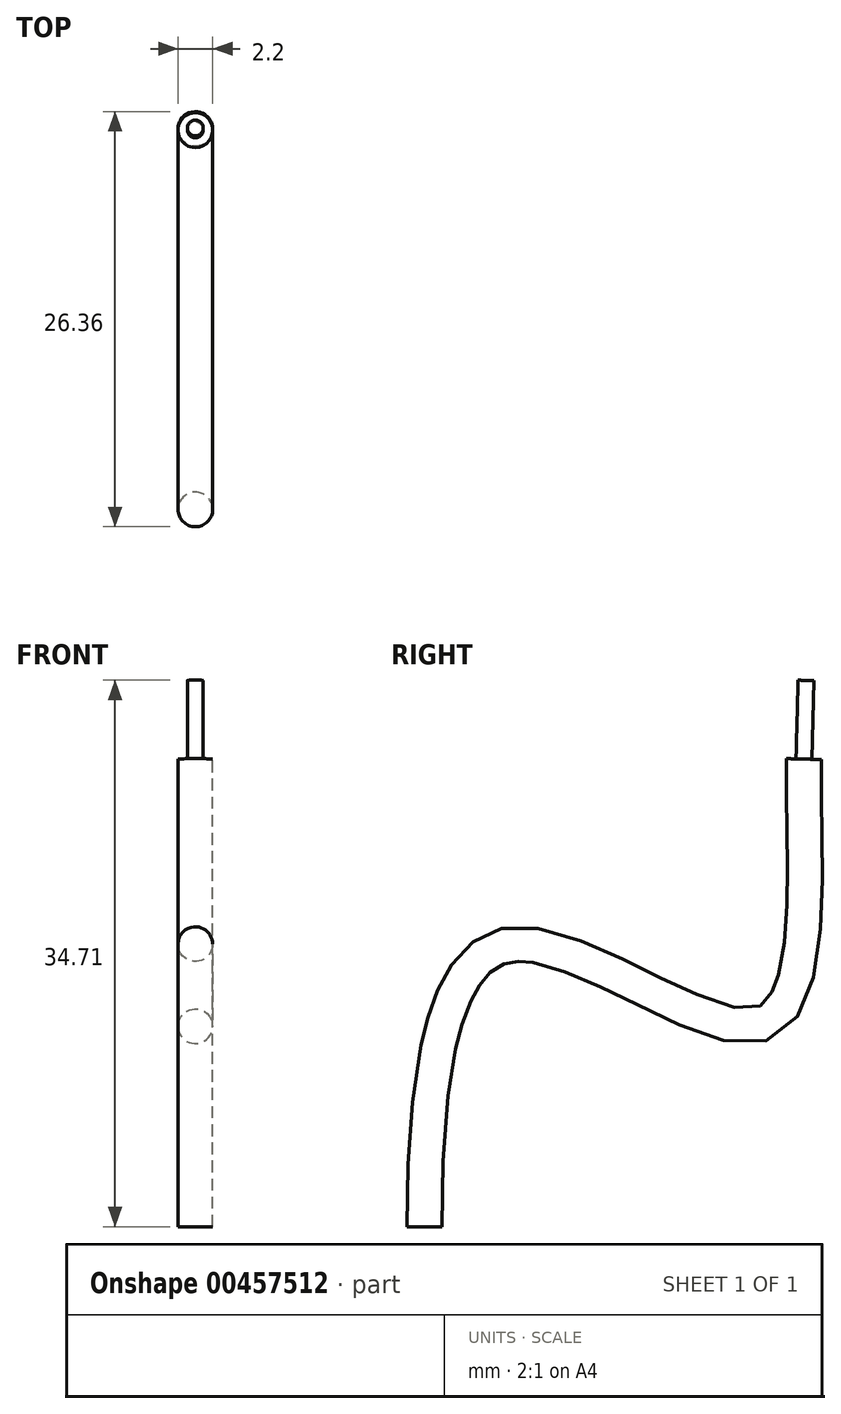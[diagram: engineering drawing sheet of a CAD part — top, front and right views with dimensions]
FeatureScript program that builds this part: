
annotation { "Feature Type Name" : "Feature", "Feature Type Description" : "" }
export const myFeature = defineFeature(function(context is Context, id is Id, definition is map)
    precondition{}
    {
        {
            var Q0;
            Q0=qCreatedBy(makeId("Top.planeOp"),FACE);
            var sketch = newSketch(context, id + "F0", { "sketchPlane" : qUnion([Q0])});
            skCircle(sketch, "E0", {"center": v(0, 0) * mm, "radius": 1.1 * mm});
            skSolve(sketch);
        }
        {
            var Q0;
            Q0=qCreatedBy(makeId("Right.planeOp"),FACE);
            var sketch = newSketch(context, id + "F1", { "sketchPlane" : qUnion([Q0])});
            skFitSpline(sketch, "E1", {"points": [v(0, 0) * mm, v(4.88, 17.8) * mm, v(21.48, 12.89) * mm, v(24.1, 29.7) * mm], "startDerivative": vector(0, 50.06) * mm, "endDerivative": vector(1.31, 50.76) * mm});
            skSolve(sketch);
        }
        {
            var Q0;
            Q0=makeQuery(id+"F0.imprint","IMPRINT",FACE,{"disambiguationData":[TD([[makeQuery(id+"F0.imprint","IMPRINT",EDGE,{"derivedFrom":sQuery(id+"F0.wireOp",EDGE,"E0")}),1.0]])]});
            var Q1;
            Q1=sQuery(id+"F1.wireOp",EDGE,"E1");
            sweep(context, id + "F2", {"profiles" : qUnion([Q0]), "path" : qUnion([Q1])});
        }
        {
            var Q0;
            Q0=makeQuery(id+"F2.opSweep","CAP_FACE",FACE,{"disambiguationData":[OSD([sQuery(id+"F0.wireOp",EDGE,"E0"),sQuery(id+"F1.wireOp",VERTEX,"E1.end")])],"isStart":false});
            var sketch = newSketch(context, id + "F3", { "sketchPlane" : qUnion([Q0])});
            skCircle(sketch, "E2", {"center": v(0, 23.32) * mm, "radius": 0.5 * mm});
            skSolve(sketch);
        }
        {
            var Q0;
            Q0=makeQuery(id+"F3.imprint","IMPRINT",FACE,{"disambiguationData":[TD([[makeQuery(id+"F3.imprint","IMPRINT",EDGE,{"derivedFrom":sQuery(id+"F3.wireOp",EDGE,"E2")}),1.0]])]});
            extrude(context, id + "F4", {"entities" : qUnion([Q0]), "operationType" : NewBodyOperationType.ADD, "depth" : 5 * mm, "offsetDistance" : 25 * mm});
        }
    });
